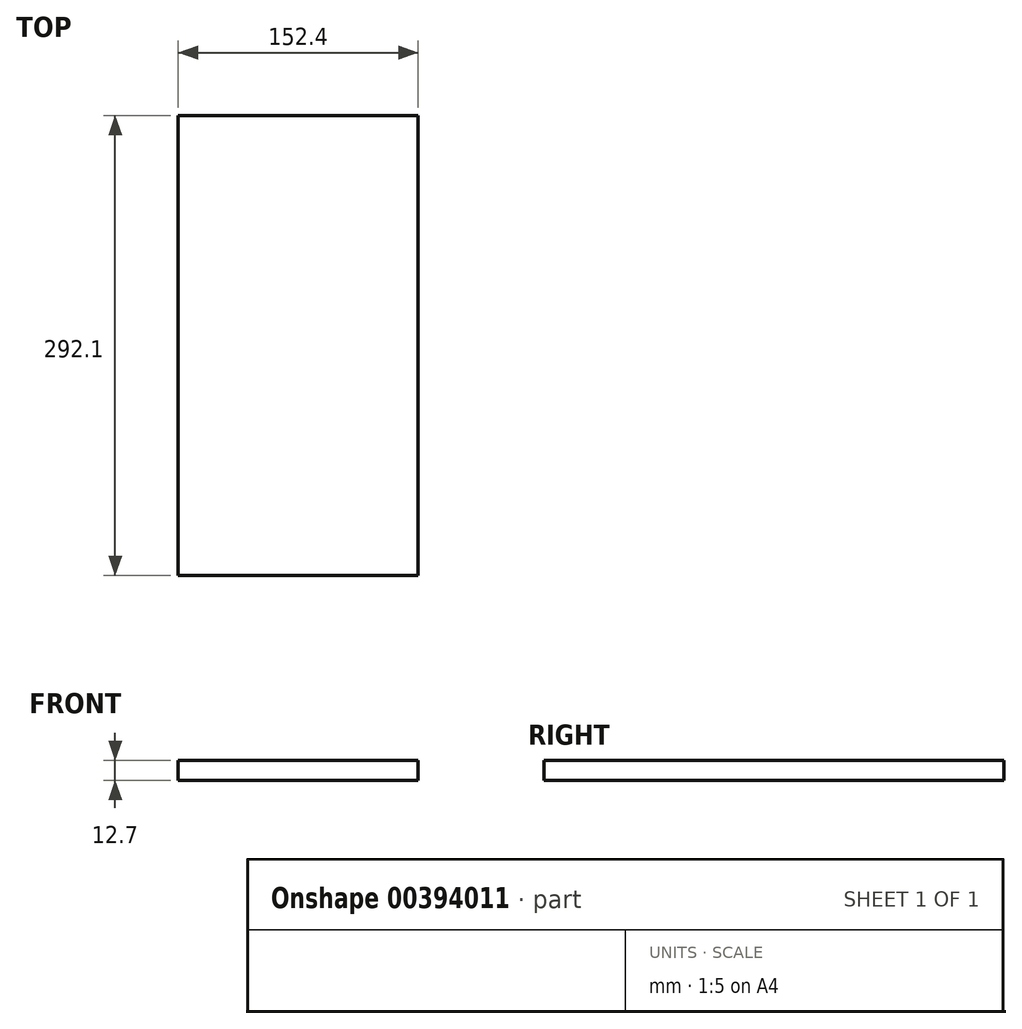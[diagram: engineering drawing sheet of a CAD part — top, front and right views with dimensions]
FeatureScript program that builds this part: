
annotation { "Feature Type Name" : "Feature", "Feature Type Description" : "" }
export const myFeature = defineFeature(function(context is Context, id is Id, definition is map)
    precondition{}
    {
        {
            var Q0;
            Q0=qCreatedBy(makeId("Top.planeOp"),FACE);
            var sketch = newSketch(context, id + "F0", { "sketchPlane" : qUnion([Q0])});
            skLineSegment(sketch, "E0.bottom", {"start": v(76.2, 146.05) * mm, "end": v(-76.2, 146.05) * mm});
            skLineSegment(sketch, "E0.top", {"start": v(76.2, -146.05) * mm, "end": v(-76.2, -146.05) * mm});
            skLineSegment(sketch, "E0.left", {"start": v(76.2, 146.05) * mm, "end": v(76.2, -146.05) * mm});
            skLineSegment(sketch, "E0.right", {"start": v(-76.2, 146.05) * mm, "end": v(-76.2, -146.05) * mm});
            skPoint(sketch, "E0.middle", {"position": v(0, 0) * mm});
            skSolve(sketch);
        }
        {
            var Q0;
            Q0=qSketchRegion(id+"F0",true);
            extrude(context, id + "F1", {"entities" : qUnion([Q0]), "depth" : 12.7 * mm});
        }
    });
